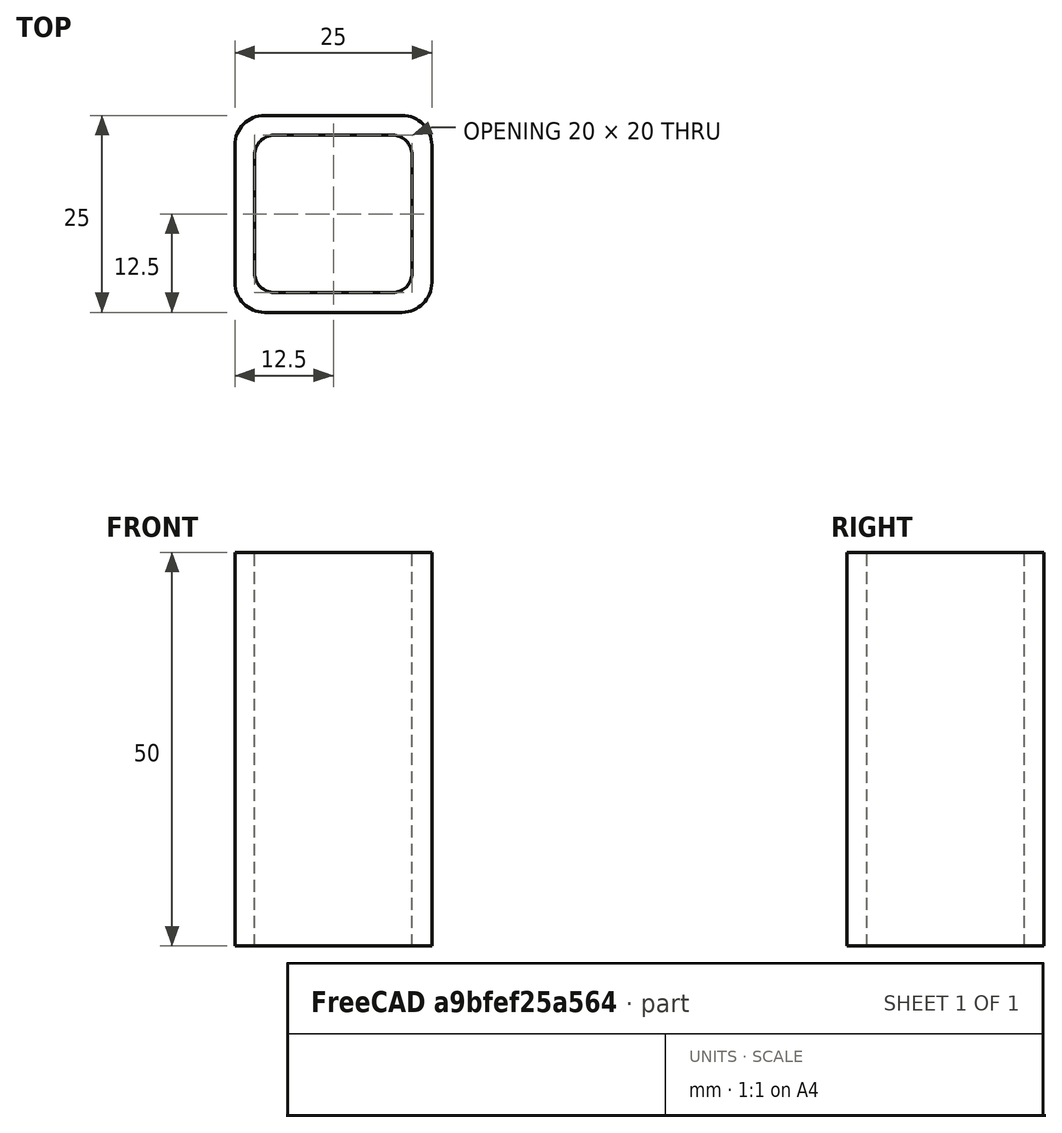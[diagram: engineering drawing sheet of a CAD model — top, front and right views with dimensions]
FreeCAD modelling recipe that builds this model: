
FCSTD DOCUMENT  (FreeCAD 0.15R4671 (Git))
Label: Square hollow section 25x25x2.5 EN10219 S235JRH
License: All rights reserved
LicenseURL: http://en.wikipedia.org/wiki/All_rights_reserved
objects: Sketcher::SketchObject×1, Part::Extrusion×1
note: 2 computed .brp shape members not serialized (recipe doc carries the construction recipe); baked Part::Feature solids carry a one-line shape summary decoded from their .brp

FEATURE [Sketcher::SketchObject] Sketch
  sketch-geometry (16):
    g0: LineSegment StartX=-7.5 StartY=10 StartZ=0 EndX=7.5 EndY=10 EndZ=0
    g1: LineSegment StartX=10 StartY=7.5 StartZ=0 EndX=10 EndY=-7.5 EndZ=0
    g2: LineSegment StartX=7.5 StartY=-10 StartZ=0 EndX=-7.5 EndY=-10 EndZ=0
    g3: LineSegment StartX=-10 StartY=-7.5 StartZ=0 EndX=-10 EndY=7.5 EndZ=0
    g4: LineSegment StartX=-8.75 StartY=12.5 StartZ=0 EndX=8.75 EndY=12.5 EndZ=0
    g5: LineSegment StartX=12.5 StartY=8.75 StartZ=0 EndX=12.5 EndY=-8.75 EndZ=0
    g6: LineSegment StartX=8.75 StartY=-12.5 StartZ=0 EndX=-8.75 EndY=-12.5 EndZ=0
    g7: LineSegment StartX=-12.5 StartY=-8.75 StartZ=0 EndX=-12.5 EndY=8.75 EndZ=0
    g8: ArcOfCircle CenterX=-7.5 CenterY=7.5 CenterZ=0 NormalX=0 NormalY=0 NormalZ=1 Radius=2.5 StartAngle=1.5708 EndAngle=3.14159
    g9: ArcOfCircle CenterX=7.5 CenterY=7.5 CenterZ=0 NormalX=0 NormalY=0 NormalZ=1 Radius=2.5 StartAngle=0 EndAngle=1.5708
    g10: ArcOfCircle CenterX=7.5 CenterY=-7.5 CenterZ=0 NormalX=0 NormalY=0 NormalZ=1 Radius=2.5 StartAngle=4.71239 EndAngle=6.28319
    g11: ArcOfCircle CenterX=-7.5 CenterY=-7.5 CenterZ=0 NormalX=0 NormalY=0 NormalZ=1 Radius=2.5 StartAngle=3.14159 EndAngle=4.71239
    g12: ArcOfCircle CenterX=8.75 CenterY=8.75 CenterZ=0 NormalX=0 NormalY=0 NormalZ=1 Radius=3.75 StartAngle=0 EndAngle=1.5708
    g13: ArcOfCircle CenterX=8.75 CenterY=-8.75 CenterZ=0 NormalX=0 NormalY=0 NormalZ=1 Radius=3.75 StartAngle=4.71239 EndAngle=6.28319
    g14: ArcOfCircle CenterX=-8.75 CenterY=-8.75 CenterZ=0 NormalX=0 NormalY=0 NormalZ=1 Radius=3.75 StartAngle=3.14159 EndAngle=4.71239
    g15: ArcOfCircle CenterX=-8.75 CenterY=8.75 CenterZ=0 NormalX=0 NormalY=0 NormalZ=1 Radius=3.75 StartAngle=1.5708 EndAngle=3.14159
  constraints (36):
    c: Horizontal(g2)
    c: Vertical(g3)
    c: Horizontal(g6)
    c: Vertical(g7)
    c: Tangent(g3,g8) = 1.5708
    c: Tangent(g0,g8) = 1.5708
    c: Tangent(g0,g9) = 1.5708
    c: Tangent(g1,g9) = 1.5708
    c: Tangent(g1,g10) = 1.5708
    c: Tangent(g2,g10) = 1.5708
    c: Tangent(g2,g11) = 1.5708
    c: Tangent(g3,g11) = 1.5708
    c: Tangent(g4,g12) = 1.5708
    c: Tangent(g5,g12) = 1.5708
    c: Tangent(g5,g13) = 1.5708
    c: Tangent(g6,g13) = 1.5708
    c: Tangent(g6,g14) = 1.5708
    c: Tangent(g7,g14) = 1.5708
    c: Tangent(g7,g15) = 1.5708
    c: Tangent(g4,g15) = 1.5708
    c: Equal(g9,g8)
    c: Equal(g9,g11)
    c: Equal(g9,g10)
    c: Equal(g12,g15)
    c: Equal(g12,g14)
    c: Equal(g12,g13)
    c: Symmetric(g4,g6,g-1)
    c: Symmetric(g7,g5,g-2)
    c: DistanceY(g4,g6) = -25
    c: DistanceX(g7,g5) = 25
    c: Symmetric(g3,g1,g-2)
    c: Symmetric(g0,g2,g-1)
    c: DistanceY(g0,g4) = 2.5
    c: DistanceX(g5,g1) = -2.5
    c: Radius(g9) = 2.5
    c: Radius(g12) = 3.75
FEATURE [Part::Extrusion] Extrude  label="Square hollow section 25x25x2.5 EN10219 S235JRH"
  Base = -> Sketch
  Dir = (0,0,50)
  Solid = true
